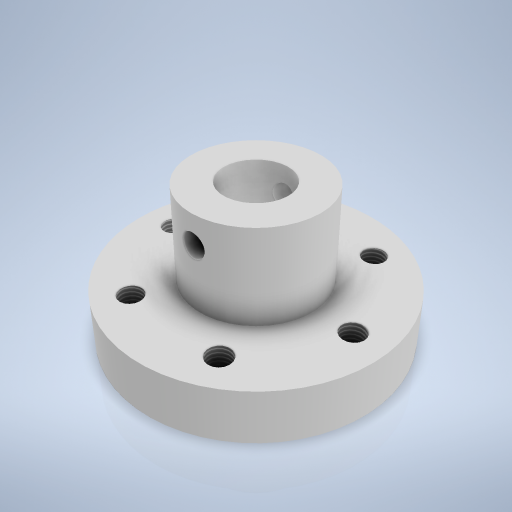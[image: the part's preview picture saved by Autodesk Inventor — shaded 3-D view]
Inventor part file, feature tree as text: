
AUTODESK INVENTOR PART (.ipt)
format: ipt  version: 2024.2 (Build 282272000, 272)  size: 303,616 bytes
history: native  units: mm
features: sketch x4, hole x2, revolve x1, extrude x1, plane x1, pattern_circular x1
ambient origin geometry x8: Origin, YZ Plane, XZ Plane, XY Plane, X Axis, Y Axis, Z Axis, Center Point
bodies: Volumenkörper1 (feature_tree)
feature tree (10):
  revolve  "Umdrehung1"
  extrude  "Extrusion1"  Depth=56.0mm
  plane  "Arbeitsebene1"
  hole  "Bohrung1"  [1 undecoded]
  hole  "Bohrung2"  [1 undecoded]
  pattern_circular  "Runde Anordnung1"  [2 undecoded]
  sketch  "Skizze1"  dims[d0=116.0mm d1=56.0mm]
  sketch  "Skizze2"  dims[d2=22.0mm d3=38.0mm]
  sketch  "Skizze3"  dims[d4=90.0deg d5=28.0mm]
  sketch  "Skizze4"  dims[d6=10.0mm d7=0.0mm d8=28.0mm d9=12.0mm d10=10.0mm d11=6.0mm d12=4.0mm d13=2.0mm d14=90.0deg d15=8.0mm d16=20.594885mm d17=88.0mm d18=30.0deg d19=30.0deg d20=10.106mm d21=24.0mm d22=4.0mm d23=2.0mm d24=90.0deg d25=8.0mm d26=20.594885mm d27=60.0mm d28=360.0deg]
note: 4 required parameter values undecoded (feature->parameter linkage not recoverable at this tier; creation-order binding heuristic only, values carry confidence <= 0.55)
